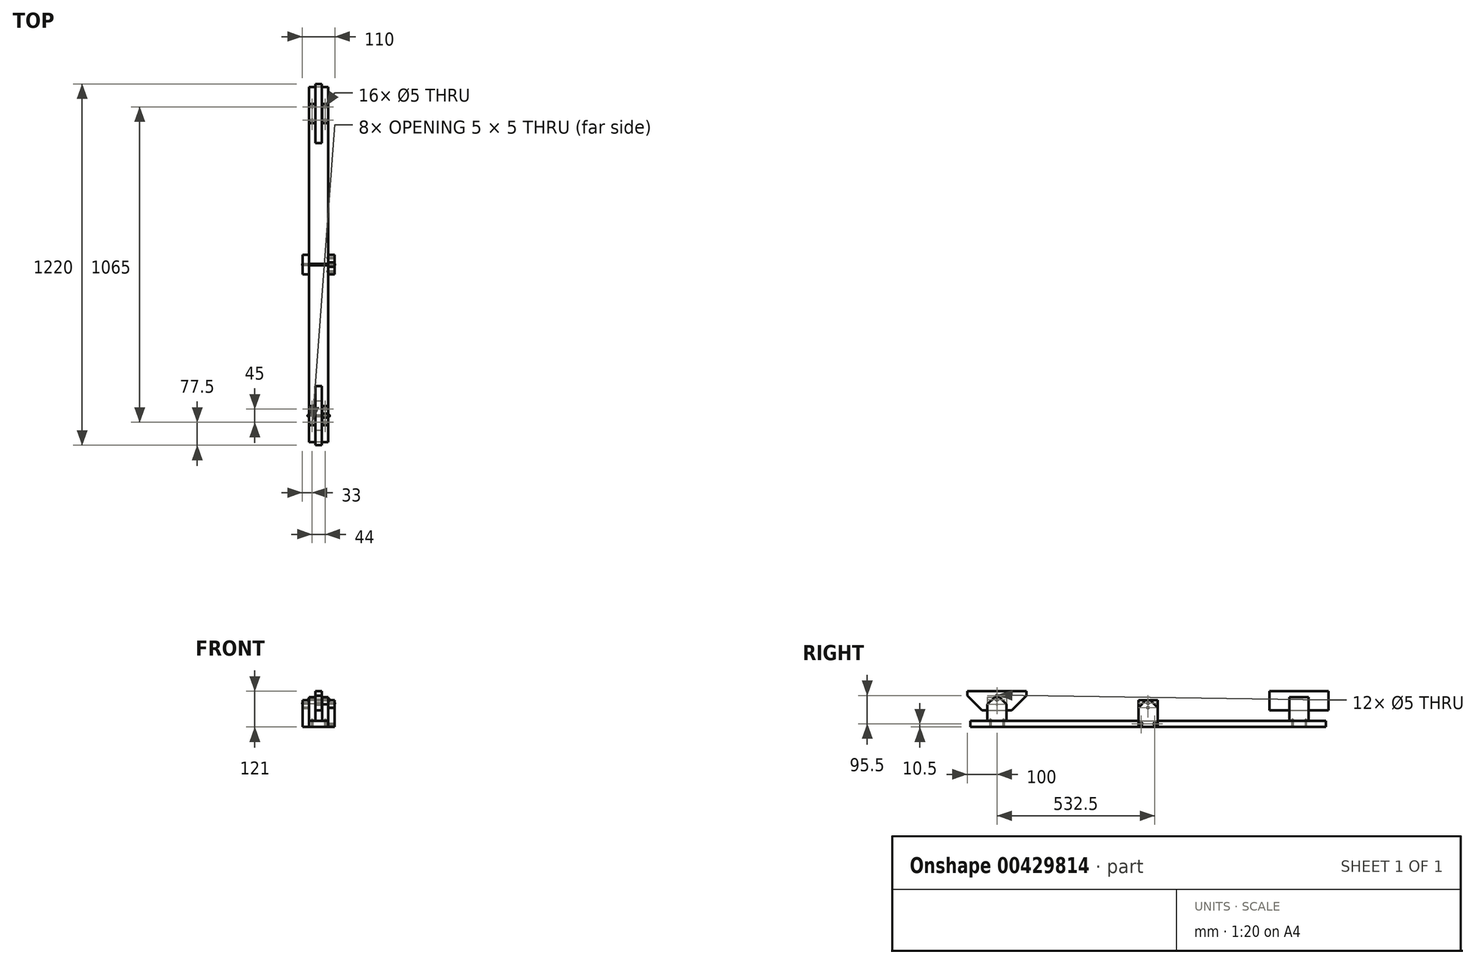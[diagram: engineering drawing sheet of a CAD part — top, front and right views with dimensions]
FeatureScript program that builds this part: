
annotation { "Feature Type Name" : "Feature", "Feature Type Description" : "" }
export const myFeature = defineFeature(function(context is Context, id is Id, definition is map)
    precondition{}
    {
        {
            var Q0;
            Q0=qCreatedBy(makeId("Top.planeOp"),FACE);
            var sketch = newSketch(context, id + "F0", { "sketchPlane" : qUnion([Q0])});
            skLineSegment(sketch, "E0.bottom", {"start": v(32.5, -600) * mm, "end": v(-32.5, -600) * mm});
            skLineSegment(sketch, "E0.top", {"start": v(32.5, 600) * mm, "end": v(-32.5, 600) * mm});
            skLineSegment(sketch, "E0.left", {"start": v(32.5, -600) * mm, "end": v(32.5, 600) * mm});
            skLineSegment(sketch, "E0.right", {"start": v(-32.5, -600) * mm, "end": v(-32.5, 600) * mm});
            skPoint(sketch, "E0.middle", {"position": v(0, 0) * mm});
            skSolve(sketch);
        }
        {
            var Q0;
            Q0 = qSketchRegion(id + "F0", true);
            extrude(context, id + "F1", {"entities" : qUnion([Q0]), "depth" : 21 * mm});
        }
        {
            var Q0;
            Q0=makeQuery(id+"F1.opExtrude","CAP_FACE",FACE,{"disambiguationData":[OSD([sQuery(id+"F0.wireOp",EDGE,"E0.bottom"),sQuery(id+"F0.wireOp",EDGE,"E0.top"),sQuery(id+"F0.wireOp",EDGE,"E0.left"),sQuery(id+"F0.wireOp",EDGE,"E0.right")])],"isStart":false});
            var sketch = newSketch(context, id + "F2", { "sketchPlane" : qUnion([Q0])});
            skLineSegment(sketch, "E1.bottom", {"start": v(-32.5, 542.5) * mm, "end": v(-11.5, 542.5) * mm});
            skLineSegment(sketch, "E1.top", {"start": v(-32.5, 477.5) * mm, "end": v(-11.5, 477.5) * mm});
            skLineSegment(sketch, "E1.left", {"start": v(-32.5, 542.5) * mm, "end": v(-32.5, 477.5) * mm});
            skLineSegment(sketch, "E1.right", {"start": v(-11.5, 542.5) * mm, "end": v(-11.5, 477.5) * mm});
            skLineSegment(sketch, "E2.bottom", {"start": v(-32.5, -542.5) * mm, "end": v(-11.5, -542.5) * mm});
            skLineSegment(sketch, "E2.top", {"start": v(-32.5, -477.5) * mm, "end": v(-11.5, -477.5) * mm});
            skLineSegment(sketch, "E2.left", {"start": v(-32.5, -542.5) * mm, "end": v(-32.5, -477.5) * mm});
            skLineSegment(sketch, "E2.right", {"start": v(-11.5, -542.5) * mm, "end": v(-11.5, -477.5) * mm});
            skLineSegment(sketch, "E3", {"start": v(-32.5, -510) * mm, "end": v(32.5, -510) * mm, "construction": true});
            skLineSegment(sketch, "E4", {"start": v(-32.5, 510) * mm, "end": v(32.5, 510) * mm, "construction": true});
            skLineSegment(sketch, "E5.MirrorCS", {"start": v(32.5, 542.5) * mm, "end": v(11.5, 542.5) * mm});
            skLineSegment(sketch, "E6.MirrorCS", {"start": v(32.5, 477.5) * mm, "end": v(11.5, 477.5) * mm});
            skLineSegment(sketch, "E7.MirrorCS", {"start": v(32.5, -477.5) * mm, "end": v(11.5, -477.5) * mm});
            skLineSegment(sketch, "E8.MirrorCS", {"start": v(32.5, -542.5) * mm, "end": v(11.5, -542.5) * mm});
            skLineSegment(sketch, "E9.MirrorCS", {"start": v(32.5, -542.5) * mm, "end": v(32.5, -477.5) * mm});
            skLineSegment(sketch, "E10.MirrorCS", {"start": v(11.5, -542.5) * mm, "end": v(11.5, -477.5) * mm});
            skLineSegment(sketch, "E11.MirrorCS", {"start": v(11.5, 542.5) * mm, "end": v(11.5, 477.5) * mm});
            skLineSegment(sketch, "E12.MirrorCS", {"start": v(32.5, 542.5) * mm, "end": v(32.5, 477.5) * mm});
            skSolve(sketch);
        }
        {
            var Q0;
            Q0 = qSketchRegion(id + "F2", true);
            extrude(context, id + "F3", {"entities" : qUnion([Q0]), "depth" : 80 * mm});
        }
        {
            var Q0;
            Q0=qCreatedBy(makeId("Right.planeOp"),FACE);
            var sketch = newSketch(context, id + "F4", { "sketchPlane" : qUnion([Q0])});
            skLineSegment(sketch, "E13.bottom", {"start": v(-610, 56) * mm, "end": v(-410, 56) * mm});
            skLineSegment(sketch, "E13.top", {"start": v(-610, 121) * mm, "end": v(-410, 121) * mm});
            skLineSegment(sketch, "E13.left", {"start": v(-610, 56) * mm, "end": v(-610, 121) * mm});
            skLineSegment(sketch, "E13.right", {"start": v(-410, 56) * mm, "end": v(-410, 121) * mm});
            skLineSegment(sketch, "E14.bottom", {"start": v(410, 56) * mm, "end": v(610, 56) * mm});
            skLineSegment(sketch, "E14.top", {"start": v(410, 121) * mm, "end": v(610, 121) * mm});
            skLineSegment(sketch, "E14.left", {"start": v(410, 56) * mm, "end": v(410, 121) * mm});
            skLineSegment(sketch, "E14.right", {"start": v(610, 56) * mm, "end": v(610, 121) * mm});
            skLineSegment(sketch, "E15", {"start": v(-542.5, 101) * mm, "end": v(-477.5, 21) * mm, "construction": true});
            skLineSegment(sketch, "E16", {"start": v(-542.5, 21) * mm, "end": v(-477.5, 101) * mm, "construction": true});
            skLineSegment(sketch, "E17", {"start": v(-610, 56) * mm, "end": v(-410, 121) * mm, "construction": true});
            skLineSegment(sketch, "E18", {"start": v(-410, 56) * mm, "end": v(-610, 121) * mm, "construction": true});
            skLineSegment(sketch, "E19", {"start": v(410, 56) * mm, "end": v(610, 121) * mm, "construction": true});
            skLineSegment(sketch, "E20", {"start": v(610, 56) * mm, "end": v(410, 121) * mm, "construction": true});
            skLineSegment(sketch, "E21", {"start": v(477.5, 101) * mm, "end": v(542.5, 21) * mm, "construction": true});
            skLineSegment(sketch, "E22", {"start": v(542.5, 101) * mm, "end": v(477.5, 21) * mm, "construction": true});
            skPoint(sketch, "E23", {"position": v(510, 88.5) * mm});
            skPoint(sketch, "E24", {"position": v(510, 61) * mm});
            skPoint(sketch, "E25", {"position": v(-510, 61) * mm});
            skPoint(sketch, "E26", {"position": v(-510, 88.5) * mm});
            skSolve(sketch);
        }
        {
            var Q0;
            Q0 = qSketchRegion(id + "F4", true);
            extrude(context, id + "F5", {"entities" : qUnion([Q0]), "endBound" : BoundingType.SYMMETRIC, "depth" : 21 * mm});
        }
        {
            var Q0;
            Q0=makeQuery(id+"F3.opExtrude","SWEPT_FACE",FACE,{"disambiguationData":[OSD([sQuery(id+"F2.wireOp",EDGE,"E9.MirrorCS")])]});
            var sketch = newSketch(context, id + "F6", { "sketchPlane" : qUnion([Q0])});
            skPoint(sketch, "E27", {"position": v(-510, 91) * mm});
            skPoint(sketch, "E28.0.1.0", {"position": v(-510, 76) * mm});
            skPoint(sketch, "E28.0.2.0", {"position": v(-510, 61) * mm});
            skPoint(sketch, "E28.0.3.0", {"position": v(-510, 46) * mm});
            skLineSegment(sketch, "E28.direction1", {"start": v(-510, 91) * mm, "end": v(-330.01, 91) * mm, "construction": true});
            skLineSegment(sketch, "E28.direction2", {"start": v(-510, 91) * mm, "end": v(-510, 76) * mm, "construction": true});
            skPoint(sketch, "E29", {"position": v(-510, 106) * mm});
            skSolve(sketch);
        }
        {
            var Q0;
            Q0=sQuery(id+"F6.wireOp",VERTEX,"E27");
            var Q1;
            Q1=makeQuery(id+"F3.opExtrude","SWEPT_BODY",BODY,{"disambiguationData":[OSD([sQuery(id+"F2.wireOp",EDGE,"E7.MirrorCS"),sQuery(id+"F2.wireOp",EDGE,"E8.MirrorCS"),sQuery(id+"F2.wireOp",EDGE,"E9.MirrorCS"),sQuery(id+"F2.wireOp",EDGE,"E10.MirrorCS")])]});
            hole(context, id + "F7", {"style" : HoleStyle.SIMPLE, "endStyle" : HoleEndStyle.THROUGH, "holeDiameter" : 5 * mm, "isTappedThrough" : true, "tappedDepth" : 12 * mm, "tapClearance" : 3, "startFromSketch" : true, "locations" : qUnion([Q0]), "scope" : qUnion([Q1])});
        }
        {
            var Q0;
            Q0=sQuery(id+"F6.wireOp",VERTEX,"E28.0.1.0");
            var Q1;
            Q1=sQuery(id+"F6.wireOp",VERTEX,"E27");
            var Q2;
            Q2=sQuery(id+"F6.wireOp",VERTEX,"E27.positionSnap0");
            var Q3;
            Q3=sQuery(id+"F6.wireOp",VERTEX,"E29");
            var Q4;
            Q4=makeQuery(id+"F5.opExtrude","SWEPT_BODY",BODY,{"disambiguationData":[OSD([sQuery(id+"F4.wireOp",EDGE,"E13.bottom"),sQuery(id+"F4.wireOp",EDGE,"E13.top"),sQuery(id+"F4.wireOp",EDGE,"E13.left"),sQuery(id+"F4.wireOp",EDGE,"E13.right")])]});
            hole(context, id + "F8", {"style" : HoleStyle.SIMPLE, "endStyle" : HoleEndStyle.THROUGH, "holeDiameter" : 5 * mm, "isTappedThrough" : true, "tappedDepth" : 12 * mm, "tapClearance" : 3, "startFromSketch" : true, "locations" : qUnion([Q0, Q1, Q2, Q3]), "scope" : qUnion([Q4])});
        }
        {
            var Q0;
            Q0=qCreatedBy(makeId("Top.planeOp"),FACE);
            var sketch = newSketch(context, id + "F9", { "sketchPlane" : qUnion([Q0])});
            skLineSegment(sketch, "E30.bottom", {"start": v(-32.5, 32.5) * mm, "end": v(-53.5, 32.5) * mm});
            skLineSegment(sketch, "E30.top", {"start": v(-32.5, -32.5) * mm, "end": v(-53.5, -32.5) * mm});
            skLineSegment(sketch, "E30.left", {"start": v(-32.5, 32.5) * mm, "end": v(-32.5, -32.5) * mm});
            skLineSegment(sketch, "E30.right", {"start": v(-53.5, 32.5) * mm, "end": v(-53.5, -32.5) * mm});
            skPoint(sketch, "E30.middle", {"position": v(-43, 0) * mm});
            skLineSegment(sketch, "E31.MirrorCS", {"start": v(53.5, 32.5) * mm, "end": v(53.5, -32.5) * mm});
            skLineSegment(sketch, "E32.MirrorCS", {"start": v(32.5, -32.5) * mm, "end": v(53.5, -32.5) * mm});
            skLineSegment(sketch, "E33.MirrorCS", {"start": v(32.5, 32.5) * mm, "end": v(32.5, -32.5) * mm});
            skPoint(sketch, "E34.MirrorP", {"position": v(43, 0) * mm});
            skLineSegment(sketch, "E35.MirrorCS", {"start": v(32.5, 32.5) * mm, "end": v(53.5, 32.5) * mm});
            skSolve(sketch);
        }
        {
            var Q0;
            Q0 = qSketchRegion(id + "F9", true);
            extrude(context, id + "F10", {"entities" : qUnion([Q0]), "depth" : 90 * mm});
        }
        {
            var Q0;
            Q0=makeQuery(id+"F10.opExtrude","SWEPT_FACE",FACE,{"disambiguationData":[OSD([sQuery(id+"F9.wireOp",EDGE,"E31.MirrorCS")])]});
            var sketch = newSketch(context, id + "F11", { "sketchPlane" : qUnion([Q0])});
            skPoint(sketch, "E36", {"position": v(0, 80) * mm});
            skPoint(sketch, "E37", {"position": v(0, 65) * mm});
            skSolve(sketch);
        }
        {
            var Q0;
            Q0=sQuery(id+"F11.wireOp",VERTEX,"E36");
            var Q1;
            Q1=sQuery(id+"F11.wireOp",VERTEX,"E37");
            var Q2;
            Q2=makeQuery(id+"F10.opExtrude","SWEPT_BODY",BODY,{"disambiguationData":[OSD([sQuery(id+"F9.wireOp",EDGE,"E30.bottom"),sQuery(id+"F9.wireOp",EDGE,"E30.top"),sQuery(id+"F9.wireOp",EDGE,"E30.left"),sQuery(id+"F9.wireOp",EDGE,"E30.right")])]});
            var Q3;
            Q3=makeQuery(id+"F10.opExtrude","SWEPT_BODY",BODY,{"disambiguationData":[OSD([sQuery(id+"F9.wireOp",EDGE,"E31.MirrorCS"),sQuery(id+"F9.wireOp",EDGE,"E32.MirrorCS"),sQuery(id+"F9.wireOp",EDGE,"E33.MirrorCS"),sQuery(id+"F9.wireOp",EDGE,"E35.MirrorCS")])]});
            hole(context, id + "F12", {"style" : HoleStyle.SIMPLE, "endStyle" : HoleEndStyle.THROUGH, "holeDiameter" : 5 * mm, "isTappedThrough" : true, "tappedDepth" : 12 * mm, "tapClearance" : 3, "startFromSketch" : true, "locations" : qUnion([Q0, Q1]), "scope" : qUnion([Q2, Q3])});
        }
        {
            var Q0;
            Q0=makeQuery(id+"F3.opExtrude","CAP_EDGE",EDGE,{"disambiguationData":[OSD([sQuery(id+"F2.wireOp",EDGE,"E8.MirrorCS")])],"isStart":false});
            var Q1;
            Q1=makeQuery(id+"F3.opExtrude","CAP_EDGE",EDGE,{"disambiguationData":[OSD([sQuery(id+"F2.wireOp",EDGE,"E7.MirrorCS")])],"isStart":false});
            var Q2;
            Q2=makeQuery(id+"F10.opExtrude","CAP_EDGE",EDGE,{"disambiguationData":[OSD([sQuery(id+"F9.wireOp",EDGE,"E32.MirrorCS")])],"isStart":false});
            var Q3;
            Q3=makeQuery(id+"F10.opExtrude","CAP_EDGE",EDGE,{"disambiguationData":[OSD([sQuery(id+"F9.wireOp",EDGE,"E35.MirrorCS")])],"isStart":false});
            chamfer(context, id + "F13", {"entities" : qUnion([Q0, Q1, Q2, Q3]), "width" : 25 * mm, "tangentPropagation" : true});
        }
        {
            var Q0;
            Q0=makeQuery(id+"F1.opExtrude","CAP_FACE",FACE,{"disambiguationData":[OSD([sQuery(id+"F0.wireOp",EDGE,"E0.bottom"),sQuery(id+"F0.wireOp",EDGE,"E0.top"),sQuery(id+"F0.wireOp",EDGE,"E0.left"),sQuery(id+"F0.wireOp",EDGE,"E0.right")])],"isStart":true});
            var sketch = newSketch(context, id + "F14", { "sketchPlane" : qUnion([Q0])});
            skPoint(sketch, "E38", {"position": v(-22, 532.5) * mm});
            skPoint(sketch, "E39", {"position": v(-22, 487.5) * mm});
            skLineSegment(sketch, "E40", {"start": v(-22, 542.5) * mm, "end": v(-22, 477.5) * mm, "construction": true});
            skLineSegment(sketch, "E41", {"start": v(-22, -477.5) * mm, "end": v(-22, -542.5) * mm, "construction": true});
            skPoint(sketch, "E42", {"position": v(-22, -487.5) * mm});
            skPoint(sketch, "E43", {"position": v(-22, -532.5) * mm});
            skPoint(sketch, "E44.MirrorP", {"position": v(22, 532.5) * mm});
            skPoint(sketch, "E45.MirrorP", {"position": v(22, 487.5) * mm});
            skPoint(sketch, "E46.MirrorP", {"position": v(22, -487.5) * mm});
            skPoint(sketch, "E47.MirrorP", {"position": v(22, -532.5) * mm});
            skSolve(sketch);
        }
        {
            var Q0;
            Q0=sQuery(id+"F14.wireOp",VERTEX,"E46.MirrorP");
            var Q1;
            Q1=sQuery(id+"F14.wireOp",VERTEX,"E47.MirrorP");
            var Q2;
            Q2=sQuery(id+"F14.wireOp",VERTEX,"E42");
            var Q3;
            Q3=sQuery(id+"F14.wireOp",VERTEX,"E43");
            var Q4;
            Q4=sQuery(id+"F14.wireOp",VERTEX,"E44.MirrorP");
            var Q5;
            Q5=sQuery(id+"F14.wireOp",VERTEX,"E45.MirrorP");
            var Q6;
            Q6=sQuery(id+"F14.wireOp",VERTEX,"E38");
            var Q7;
            Q7=sQuery(id+"F14.wireOp",VERTEX,"E39");
            var Q8;
            Q8=makeQuery(id+"F3.opExtrude","SWEPT_BODY",BODY,{"disambiguationData":[OSD([sQuery(id+"F2.wireOp",EDGE,"E7.MirrorCS"),sQuery(id+"F2.wireOp",EDGE,"E8.MirrorCS"),sQuery(id+"F2.wireOp",EDGE,"E9.MirrorCS"),sQuery(id+"F2.wireOp",EDGE,"E10.MirrorCS")])]});
            var Q9;
            Q9=makeQuery(id+"F1.opExtrude","SWEPT_BODY",BODY,{"disambiguationData":[OSD([sQuery(id+"F0.wireOp",EDGE,"E0.bottom"),sQuery(id+"F0.wireOp",EDGE,"E0.top"),sQuery(id+"F0.wireOp",EDGE,"E0.left"),sQuery(id+"F0.wireOp",EDGE,"E0.right")])]});
            var Q10;
            Q10=makeQuery(id+"F3.opExtrude","SWEPT_BODY",BODY,{"disambiguationData":[OSD([sQuery(id+"F2.wireOp",EDGE,"E1.bottom"),sQuery(id+"F2.wireOp",EDGE,"E1.top"),sQuery(id+"F2.wireOp",EDGE,"E1.left"),sQuery(id+"F2.wireOp",EDGE,"E1.right")])]});
            var Q11;
            Q11=makeQuery(id+"F3.opExtrude","SWEPT_BODY",BODY,{"disambiguationData":[OSD([sQuery(id+"F2.wireOp",EDGE,"E2.bottom"),sQuery(id+"F2.wireOp",EDGE,"E2.top"),sQuery(id+"F2.wireOp",EDGE,"E2.left"),sQuery(id+"F2.wireOp",EDGE,"E2.right")])]});
            var Q12;
            Q12=makeQuery(id+"F3.opExtrude","SWEPT_BODY",BODY,{"disambiguationData":[OSD([sQuery(id+"F2.wireOp",EDGE,"E5.MirrorCS"),sQuery(id+"F2.wireOp",EDGE,"E6.MirrorCS"),sQuery(id+"F2.wireOp",EDGE,"E11.MirrorCS"),sQuery(id+"F2.wireOp",EDGE,"E12.MirrorCS")])]});
            hole(context, id + "F15", {"style" : HoleStyle.C_SINK, "endStyle" : HoleEndStyle.BLIND, "standardTappedOrClearance" : lookupTablePath({ "standard" : "ISO", "size" : "5", "type" : "Drilled" }), "standardBlindInLast" : lookupTablePath({ "standard" : "ISO", "size" : "5", "type" : "Drilled" }), "holeDiameter" : 5 * mm, "cSinkDiameter" : 8.3 * mm, "cSinkAngle" : 90 * degree, "holeDepth" : 25 * mm, "isTappedThrough" : true, "tappedDepth" : 12 * mm, "tapClearance" : 3, "startFromSketch" : true, "locations" : qUnion([Q0, Q1, Q2, Q3, Q4, Q5, Q6, Q7]), "scope" : qUnion([Q8, Q9, Q10, Q11, Q12])});
        }
        {
            var Q0;
            Q0=makeQuery(id+"F10.opExtrude","SWEPT_FACE",FACE,{"disambiguationData":[OSD([sQuery(id+"F9.wireOp",EDGE,"E31.MirrorCS")])]});
            var sketch = newSketch(context, id + "F16", { "sketchPlane" : qUnion([Q0])});
            skPoint(sketch, "E48", {"position": v(-22.5, 10.5) * mm});
            skPoint(sketch, "E49.MirrorP", {"position": v(22.5, 10.5) * mm});
            skSolve(sketch);
        }
        {
            var Q0;
            Q0=sQuery(id+"F16.wireOp",VERTEX,"E48");
            var Q1;
            Q1=sQuery(id+"F16.wireOp",VERTEX,"E49.MirrorP");
            var Q2;
            Q2=makeQuery(id+"F1.opExtrude","SWEPT_BODY",BODY,{"disambiguationData":[OSD([sQuery(id+"F0.wireOp",EDGE,"E0.bottom"),sQuery(id+"F0.wireOp",EDGE,"E0.top"),sQuery(id+"F0.wireOp",EDGE,"E0.left"),sQuery(id+"F0.wireOp",EDGE,"E0.right")])]});
            var Q3;
            Q3=makeQuery(id+"F10.opExtrude","SWEPT_BODY",BODY,{"disambiguationData":[OSD([sQuery(id+"F9.wireOp",EDGE,"E31.MirrorCS"),sQuery(id+"F9.wireOp",EDGE,"E32.MirrorCS"),sQuery(id+"F9.wireOp",EDGE,"E33.MirrorCS"),sQuery(id+"F9.wireOp",EDGE,"E35.MirrorCS")])]});
            hole(context, id + "F17", {"style" : HoleStyle.C_SINK, "endStyle" : HoleEndStyle.BLIND, "standardTappedOrClearance" : lookupTablePath({ "standard" : "ISO", "size" : "5", "type" : "Drilled" }), "standardBlindInLast" : lookupTablePath({ "standard" : "ISO", "size" : "5", "type" : "Drilled" }), "holeDiameter" : 5 * mm, "cSinkDiameter" : 8.3 * mm, "cSinkAngle" : 90 * degree, "holeDepth" : 25 * mm, "isTappedThrough" : true, "tappedDepth" : 12 * mm, "tapClearance" : 3, "startFromSketch" : true, "locations" : qUnion([Q0, Q1]), "scope" : qUnion([Q2, Q3])});
        }
        {
            var Q0;
            Q0=qCreatedBy(makeId("Right.planeOp"),FACE);
            var sketch = newSketch(context, id + "F18", { "sketchPlane" : qUnion([Q0])});
            skCircle(sketch, "E50", {"center": v(0, 80) * mm, "radius": 2 * mm});
            skSolve(sketch);
        }
        {
            var Q0;
            Q0 = qSketchRegion(id + "F18", true);
            extrude(context, id + "F19", {"entities" : qUnion([Q0]), "endBound" : BoundingType.SYMMETRIC, "depth" : 110 * mm});
        }
        {
            var Q0;
            Q0=qCreatedBy(makeId("Right.planeOp"),FACE);
            var sketch = newSketch(context, id + "F20", { "sketchPlane" : qUnion([Q0])});
            skCircle(sketch, "E51", {"center": v(-510, 91) * mm, "radius": 2 * mm});
            skSolve(sketch);
        }
        {
            var Q0;
            Q0 = qSketchRegion(id + "F20", true);
            extrude(context, id + "F21", {"entities" : qUnion([Q0]), "endBound" : BoundingType.SYMMETRIC, "depth" : 75 * mm});
        }
        {
            var Q0;
            Q0=makeQuery(id+"F5.opExtrude","SWEPT_EDGE",EDGE,{"disambiguationData":[OSD([sQuery(id+"F4.wireOp",EDGE,"E13.bottom"),sQuery(id+"F4.wireOp",EDGE,"E13.left")])]});
            var Q1;
            Q1=makeQuery(id+"F5.opExtrude","SWEPT_EDGE",EDGE,{"disambiguationData":[OSD([sQuery(id+"F4.wireOp",EDGE,"E13.bottom"),sQuery(id+"F4.wireOp",EDGE,"E13.right")])]});
            chamfer(context, id + "F22", {"entities" : qUnion([Q0, Q1]), "width" : 50 * mm, "tangentPropagation" : true});
        }
    });
